# Revit family: HD066-2016.05.17-BT-Rev. Natura
name_source: partatom
category: Generic Models
revit_build: Autodesk Revit 2016 (Build: 20150714_1515(x64)
units: mm (PartAtom-declared; Revit-internal decimal feet)

## family parameters
Always vertical = Yes
Can host rebar = No
Cut with Voids When Loaded = No
Part Type = Normal
Room Calculation Point = No
Round Connector Dimension = Use Diameter
Shared = No
Work Plane-Based = No

## types (1)
- Productos HD
    BT_Alto = 290-604 modulo maximo
    BT_Ancho = 16 mm (espesor)
    BT_Codigo_Origen = HD066
    BT_Color = Enchapados: Coigüe Chocolate, Laricina, Nogal Amazónico, Nogal Ceniza, Coigüe,

Teca Italiana, Peral, Maple.
    BT_Código_Linea = A pedido
    BT_Descripcion = Revestimiento Natura
    BT_EETT = El panel deberá tener una geometría rectangular y plana con

dimensiones máximas de 288x2400 mm, fabricado en madera

aglomerada HR100 (resistente a la humedad).

El panel es enchapado en ambas caras con una lámina de melamina

logrando un espesor total de 18 mm.

Para su instalación se considera el uso de un soporte especial, de 88

x88 mm, materialidad aluzinc en espesor 0.8 mm, el cual se fija a un

perfil omega especial de aluzinc en espesor 0.6 mm (altura 19 mm,

ancho inferior 66 mm y ancho superior 40 mm) y un perfil J especial de

dimensiones 46x10x6 mm, materialidad aluzinc en espesor 1mm.

El panel tiene una terminación ranurada por su cara frontal y perforada

por la trascara, esta última cubierta con viledon.

Opciones de ranurado estándar: 14/2 – 22/2

Alternativas de enchapado:

Coigüe Chocolate, Laricina, Nogal Amazónico, Nogal Ceniza, Coigüe,

Teca Italiana, Peral, Maple.
    BT_Elemento = Paneles y revestimientos verticales
    BT_Especialidad = Arquitectura
    BT_Fabricante = Hunter Douglas
    BT_Itemizado_Estandar_CDT = D 03 03 01
    BT_Marca = Hunter Douglas
    BT_MasterFormat® = 07 42 13
    BT_Material = Madera
    BT_Nombre_Comercial = Revestimiento Natura
    BT_Nombre_Corto = Revestimiento Natura
    BT_Nombre_Tecnico = Revestimiento Natura
    BT_Peso = 18.9 kgf/m2
    BT_Profundidad = 1200-1800-2400 mm largo
    BT_SKU = 4600
    BT_Uso = Interior
    BT_Web_del_Producto = http://www.hunterdouglas.cl
    ID_Objeto = BT_F_F_688
    ID_Source = BIMTOOL
    Madera = Default Wall
    Material = Metal

## geometry (parser evidence)
native form markers: Sweep x36
no freeform markers — native parametric forms only
